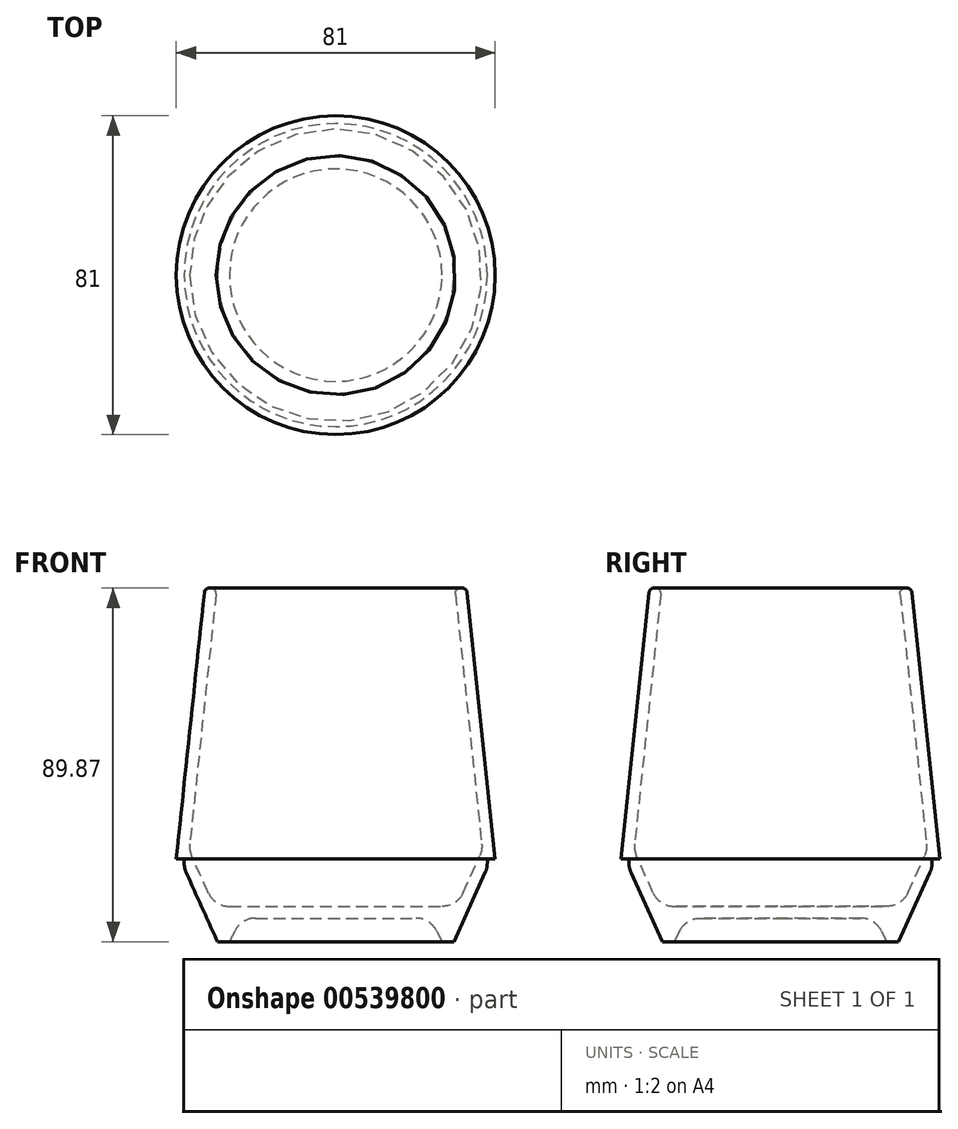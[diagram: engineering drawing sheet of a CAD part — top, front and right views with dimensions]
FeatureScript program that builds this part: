
annotation { "Feature Type Name" : "Feature", "Feature Type Description" : "" }
export const myFeature = defineFeature(function(context is Context, id is Id, definition is map)
    precondition{}
    {
        {
            var Q0;
            Q0=qCreatedBy(makeId("Front.planeOp"),FACE);
            var sketch = newSketch(context, id + "F0", { "sketchPlane" : qUnion([Q0])});
            skLineSegment(sketch, "E0", {"start": v(0, 6) * mm, "end": v(20.36, 6) * mm});
            skLineSegment(sketch, "E1", {"start": v(25.63, 2.75) * mm, "end": v(27, 0) * mm});
            skLineSegment(sketch, "E2", {"start": v(27, 0) * mm, "end": v(30, 0) * mm});
            skLineSegment(sketch, "E3", {"start": v(30, 0) * mm, "end": v(37.97, 17.57) * mm});
            skLineSegment(sketch, "E4", {"start": v(38.5, 20) * mm, "end": v(38.5, 21) * mm});
            skLineSegment(sketch, "E5", {"start": v(38.5, 21) * mm, "end": v(40.5, 21) * mm});
            skLineSegment(sketch, "E6", {"start": v(40.5, 21) * mm, "end": v(33.38, 88.7) * mm});
            skLineSegment(sketch, "E7", {"start": v(31.95, 89.86) * mm, "end": v(31.56, 89.82) * mm});
            skLineSegment(sketch, "E8", {"start": v(30.4, 88.4) * mm, "end": v(37.08, 24.82) * mm});
            skLineSegment(sketch, "E9", {"start": v(36.59, 21.77) * mm, "end": v(32.36, 12.45) * mm});
            skLineSegment(sketch, "E10", {"start": v(27, 9) * mm, "end": v(0, 9) * mm});
            skLineSegment(sketch, "E11", {"start": v(0, 9) * mm, "end": v(0, 6) * mm});
            skPoint(sketch, "E12.visualSharp", {"position": v(24, 6) * mm});
            skArc(sketch, "E12.filletArc", {"start": v(25.63, 2.75) * mm, "mid": v(23.46, 5.12) * mm, "end": v(20.36, 6) * mm});
            skPoint(sketch, "E13.visualSharp", {"position": v(30.8, 9) * mm});
            skArc(sketch, "E13.filletArc", {"start": v(27, 9) * mm, "mid": v(30.19, 9.94) * mm, "end": v(32.36, 12.45) * mm});
            skPoint(sketch, "E14.visualSharp", {"position": v(37.25, 23.23) * mm});
            skArc(sketch, "E14.filletArc", {"start": v(36.59, 21.77) * mm, "mid": v(37.04, 23.26) * mm, "end": v(37.08, 24.82) * mm});
            skPoint(sketch, "E15.visualSharp", {"position": v(38.5, 18.73) * mm});
            skArc(sketch, "E15.filletArc", {"start": v(37.97, 17.57) * mm, "mid": v(38.37, 18.76) * mm, "end": v(38.5, 20) * mm});
            skPoint(sketch, "E16.visualSharp", {"position": v(33.25, 90) * mm});
            skArc(sketch, "E16.filletArc", {"start": v(33.38, 88.7) * mm, "mid": v(32.9, 89.58) * mm, "end": v(31.95, 89.86) * mm});
            skPoint(sketch, "E17.visualSharp", {"position": v(30.26, 89.69) * mm});
            skArc(sketch, "E17.filletArc", {"start": v(31.56, 89.82) * mm, "mid": v(30.68, 89.35) * mm, "end": v(30.4, 88.4) * mm});
            skLineSegment(sketch, "E18", {"start": v(40.5, 21) * mm, "end": v(40.5, 90) * mm, "construction": true});
            skLineSegment(sketch, "E19", {"start": v(0, 0) * mm, "end": v(0, 88.7) * mm, "construction": true});
            skSolve(sketch);
        }
        {
            var Q0;
            Q0=qSketchRegion(id+"F0",true);
            var Q1;
            Q1=sQuery(id+"F0.wireOp",EDGE,"E19");
            revolve(context, id + "F1", {"entities" : qUnion([Q0]), "axis" : qUnion([Q1]), "revolveType" : RevolveType.FULL});
        }
    });
